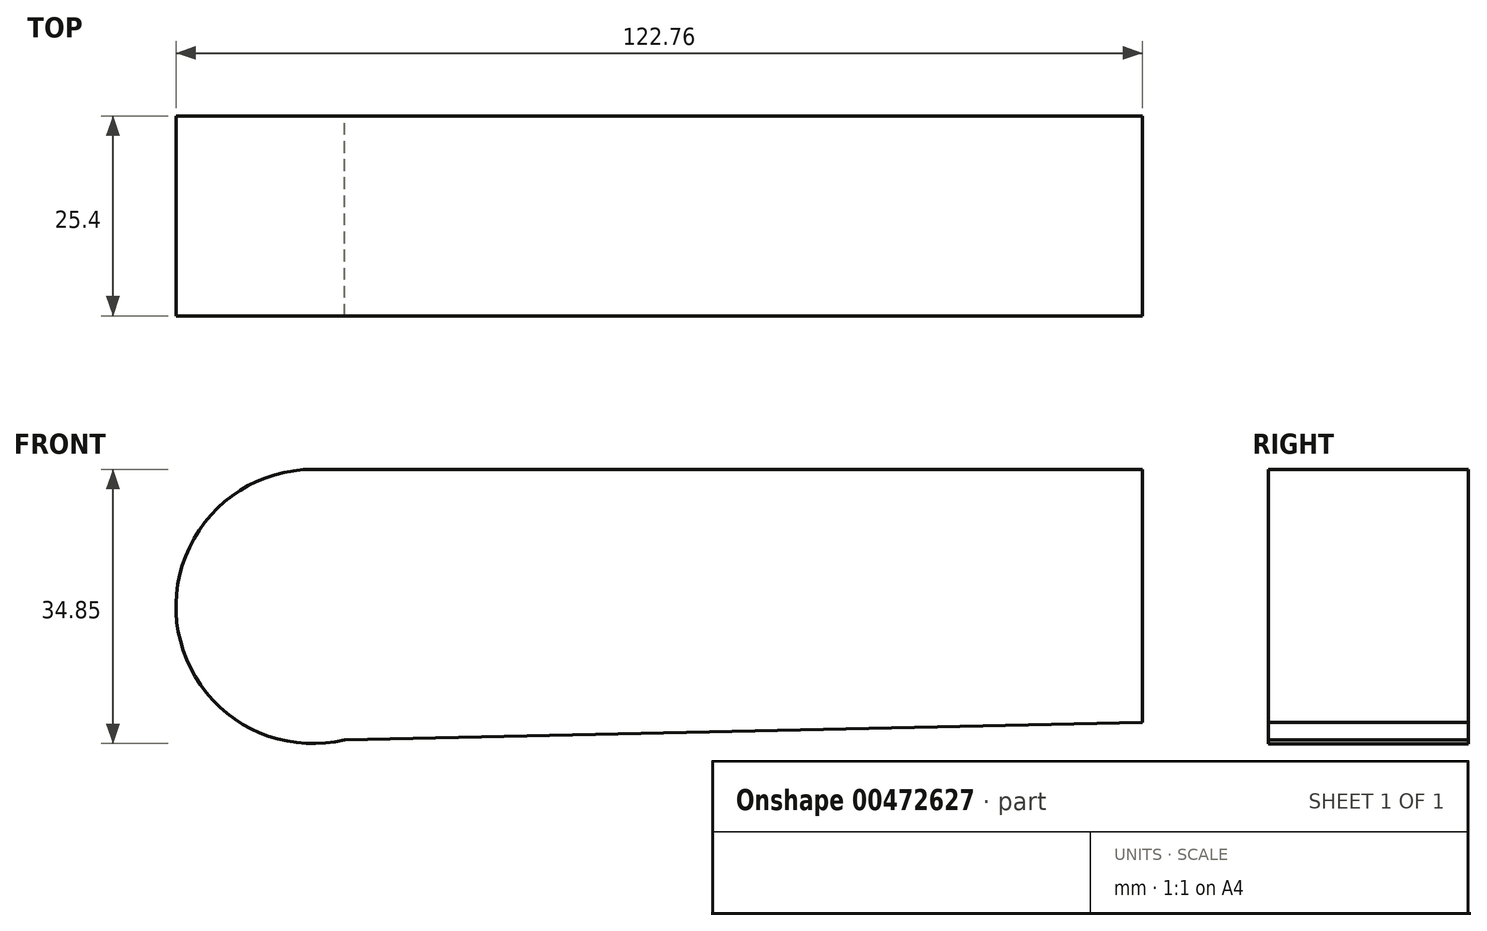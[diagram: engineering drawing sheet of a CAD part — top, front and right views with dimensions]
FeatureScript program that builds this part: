
annotation { "Feature Type Name" : "Feature", "Feature Type Description" : "" }
export const myFeature = defineFeature(function(context is Context, id is Id, definition is map)
    precondition{}
    {
        {
            var Q0;
            Q0=qCreatedBy(makeId("Front.planeOp"),FACE);
            var sketch = newSketch(context, id + "F0", { "sketchPlane" : qUnion([Q0])});
            skLineSegment(sketch, "E0", {"start": v(-53.88, 22.52) * mm, "end": v(51.46, 22.52) * mm});
            skLineSegment(sketch, "E1", {"start": v(51.46, 22.52) * mm, "end": v(51.46, -9.65) * mm});
            skLineSegment(sketch, "E2", {"start": v(-49.86, -11.86) * mm, "end": v(51.46, -9.65) * mm});
            skArc(sketch, "E3", {"start": v(-53.88, 22.52) * mm, "mid": v(-71.18, 3.07) * mm, "end": v(-49.86, -11.86) * mm});
            skSolve(sketch);
        }
        {
            var Q0;
            Q0=makeQuery(id+"F0.imprint","IMPRINT",FACE,{"disambiguationData":[TD([[makeQuery(id+"F0.imprint","IMPRINT",EDGE,{"derivedFrom":sQuery(id+"F0.wireOp",EDGE,"E0")}),-1.0]])]});
            extrude(context, id + "F1", {"entities" : qUnion([Q0]), "depth" : 25.4 * mm});
        }
    });
